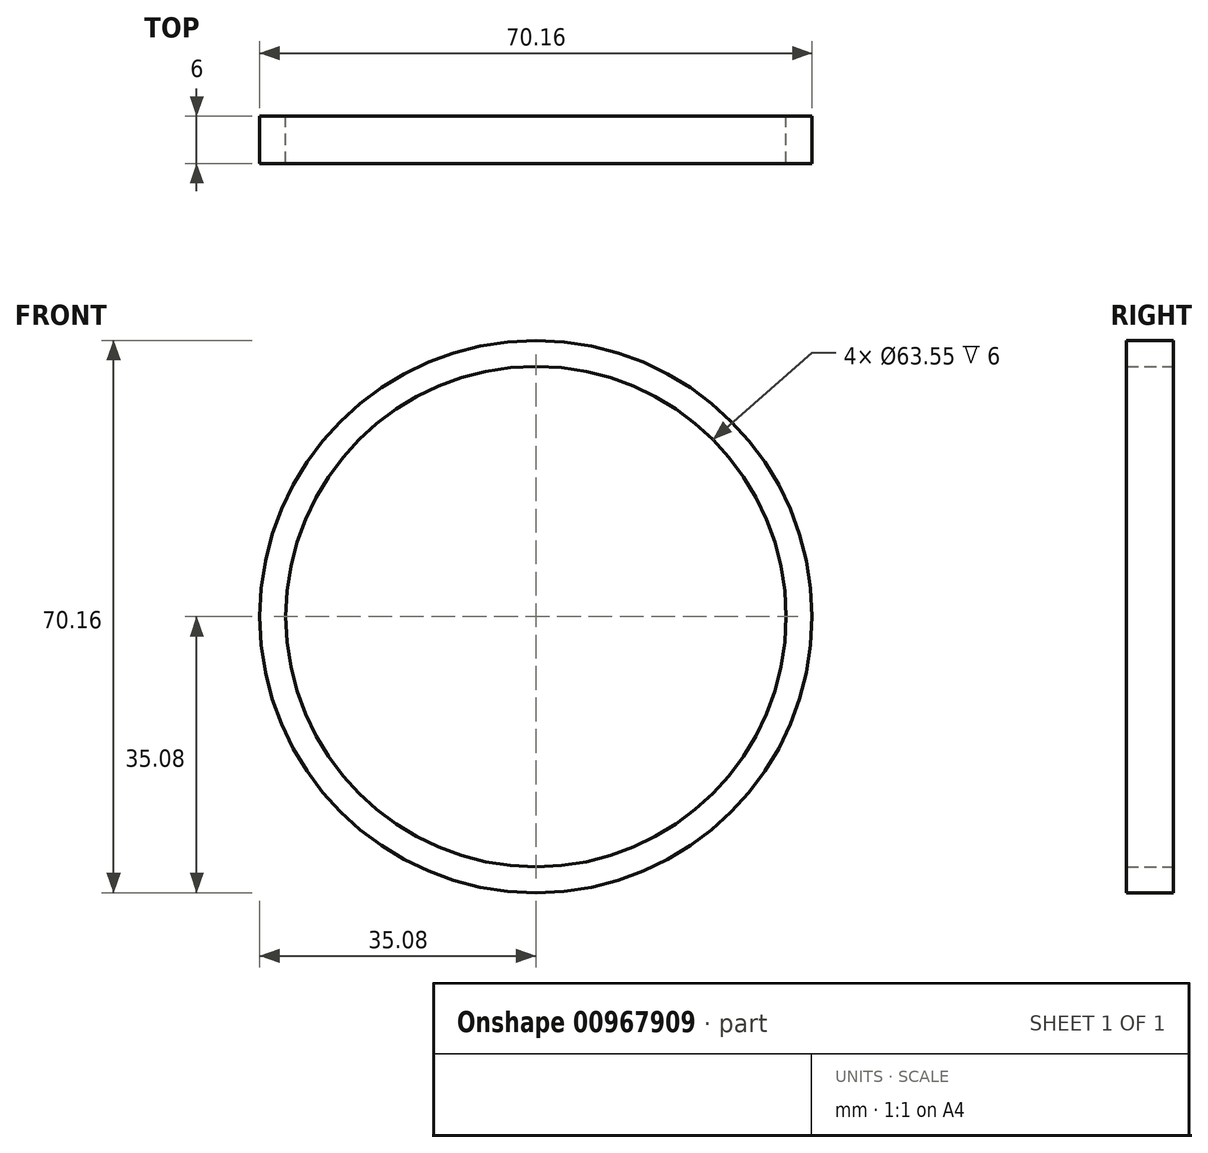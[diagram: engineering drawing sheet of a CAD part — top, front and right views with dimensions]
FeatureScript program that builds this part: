
annotation { "Feature Type Name" : "Feature", "Feature Type Description" : "" }
export const myFeature = defineFeature(function(context is Context, id is Id, definition is map)
    precondition{}
    {
        {
            var Q0;
            Q0=qCreatedBy(makeId("Front.planeOp"),FACE);
            var sketch = newSketch(context, id + "F0", { "sketchPlane" : qUnion([Q0])});
            skCircle(sketch, "E0", {"center": v(0, 0) * mm, "radius": 35.08 * mm});
            skCircle(sketch, "E1", {"center": v(0, 0) * mm, "radius": 31.77 * mm});
            skSolve(sketch);
        }
        {
            var Q0;
            Q0 = qSketchRegion(id + "F0", true);
            extrude(context, id + "F1", {"entities" : qUnion([Q0]), "depth" : 6 * mm, "offsetDistance" : 25 * mm, "symmetric" : true});
        }
    });
